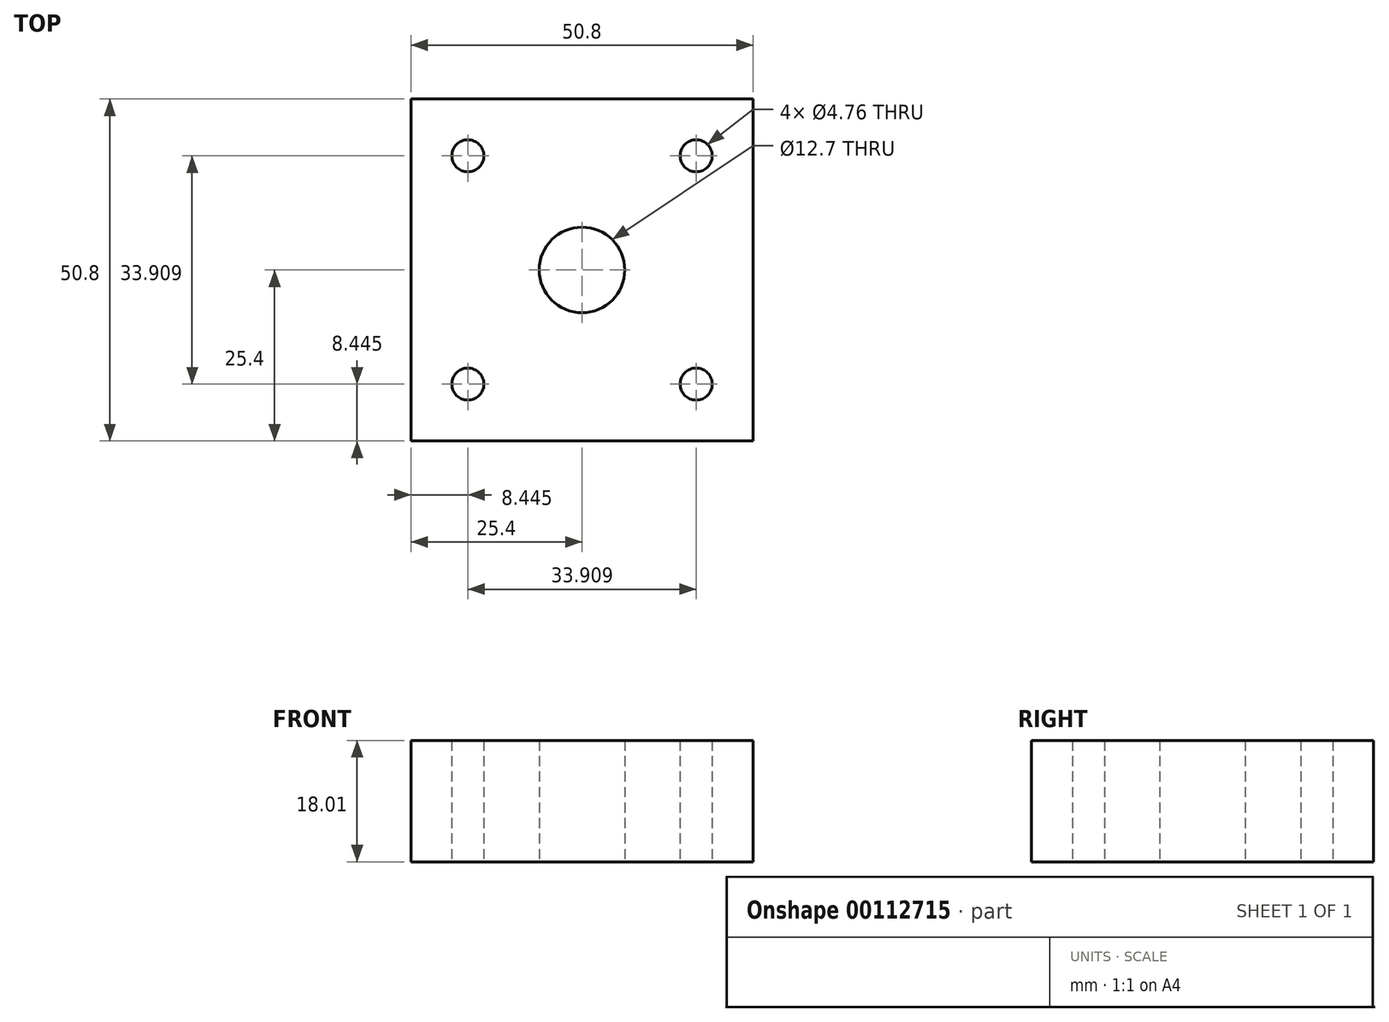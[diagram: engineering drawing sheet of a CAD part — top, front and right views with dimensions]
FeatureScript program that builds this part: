
annotation { "Feature Type Name" : "Feature", "Feature Type Description" : "" }
export const myFeature = defineFeature(function(context is Context, id is Id, definition is map)
    precondition{}
    {
        {
            var Q0;
            Q0=qCreatedBy(makeId("Top.planeOp"),FACE);
            var sketch = newSketch(context, id + "F0", { "sketchPlane" : qUnion([Q0])});
            skLineSegment(sketch, "E0.bottom", {"start": v(25.4, -25.4) * mm, "end": v(-25.4, -25.4) * mm});
            skLineSegment(sketch, "E0.top", {"start": v(25.4, 25.4) * mm, "end": v(-25.4, 25.4) * mm});
            skLineSegment(sketch, "E0.left", {"start": v(25.4, -25.4) * mm, "end": v(25.4, 25.4) * mm});
            skLineSegment(sketch, "E0.right", {"start": v(-25.4, -25.4) * mm, "end": v(-25.4, 25.4) * mm});
            skPoint(sketch, "E0.middle", {"position": v(0, 0) * mm});
            skLineSegment(sketch, "E1.bottom", {"start": v(16.95, 16.95) * mm, "end": v(-16.95, 16.95) * mm, "construction": true});
            skLineSegment(sketch, "E1.top", {"start": v(16.95, -16.95) * mm, "end": v(-16.95, -16.95) * mm, "construction": true});
            skLineSegment(sketch, "E1.left", {"start": v(16.95, 16.95) * mm, "end": v(16.95, -16.95) * mm, "construction": true});
            skLineSegment(sketch, "E1.right", {"start": v(-16.95, 16.95) * mm, "end": v(-16.95, -16.95) * mm, "construction": true});
            skCircle(sketch, "E2", {"center": v(0, 0) * mm, "radius": 6.35 * mm});
            skCircle(sketch, "E3", {"center": v(-16.95, 16.95) * mm, "radius": 8.45 * mm, "construction": true});
            skCircle(sketch, "E4", {"center": v(-16.95, 16.95) * mm, "radius": 2.38 * mm});
            skCircle(sketch, "E5", {"center": v(16.95, 16.95) * mm, "radius": 2.38 * mm});
            skCircle(sketch, "E6", {"center": v(-16.95, -16.95) * mm, "radius": 2.38 * mm});
            skCircle(sketch, "E7", {"center": v(16.95, -16.95) * mm, "radius": 2.38 * mm});
            skSolve(sketch);
        }
        {
            var Q0;
            Q0=qSketchRegion(id+"F0",true);
            extrude(context, id + "F1", {"entities" : qUnion([Q0]), "depth" : 18 * mm});
        }
    });
